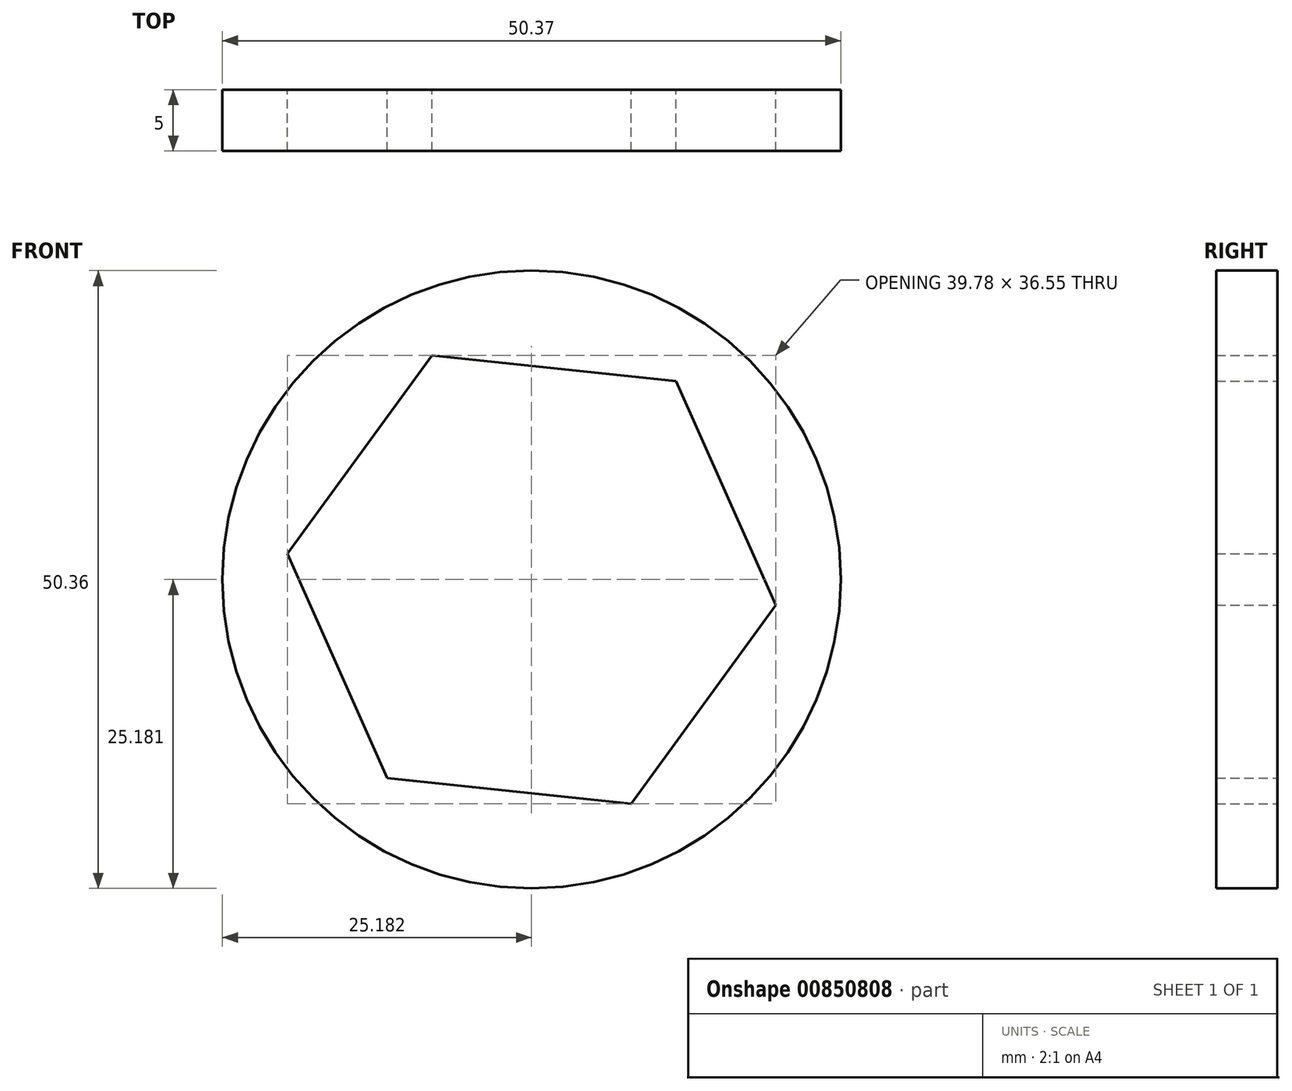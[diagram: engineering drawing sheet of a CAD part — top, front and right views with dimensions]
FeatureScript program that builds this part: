
annotation { "Feature Type Name" : "Feature", "Feature Type Description" : "" }
export const myFeature = defineFeature(function(context is Context, id is Id, definition is map)
    precondition{}
    {
        {
            var Q0;
            Q0=qCreatedBy(makeId("Front.planeOp"),FACE);
            var sketch = newSketch(context, id + "F0", { "sketchPlane" : qUnion([Q0])});
            skCircle(sketch, "E0.cCircle", {"center": v(-5.99, 8.36) * mm, "radius": 17.32 * mm, "construction": true});
            skLineSegment(sketch, "E0.0", {"start": v(13.9, 6.26) * mm, "end": v(2.14, -9.91) * mm});
            skLineSegment(sketch, "E0.1", {"start": v(2.14, -9.91) * mm, "end": v(-17.75, -7.81) * mm});
            skLineSegment(sketch, "E0.2", {"start": v(-17.75, -7.81) * mm, "end": v(-25.88, 10.46) * mm});
            skLineSegment(sketch, "E0.3", {"start": v(-25.88, 10.46) * mm, "end": v(-14.11, 26.64) * mm});
            skLineSegment(sketch, "E0.4", {"start": v(-14.11, 26.64) * mm, "end": v(5.78, 24.54) * mm});
            skLineSegment(sketch, "E0.5", {"start": v(5.78, 24.54) * mm, "end": v(13.9, 6.26) * mm});
            skPoint(sketch, "E0.0.midPoint", {"position": v(8.02, -1.83) * mm});
            skCircle(sketch, "E1", {"center": v(-5.99, 8.36) * mm, "radius": 25.18 * mm});
            skSolve(sketch);
        }
        {
            var Q0;
            Q0 = qSketchRegion(id + "F0", true);
            extrude(context, id + "F1", {"entities" : qUnion([Q0]), "depth" : 5 * mm, "offsetDistance" : 25 * mm});
        }
    });
